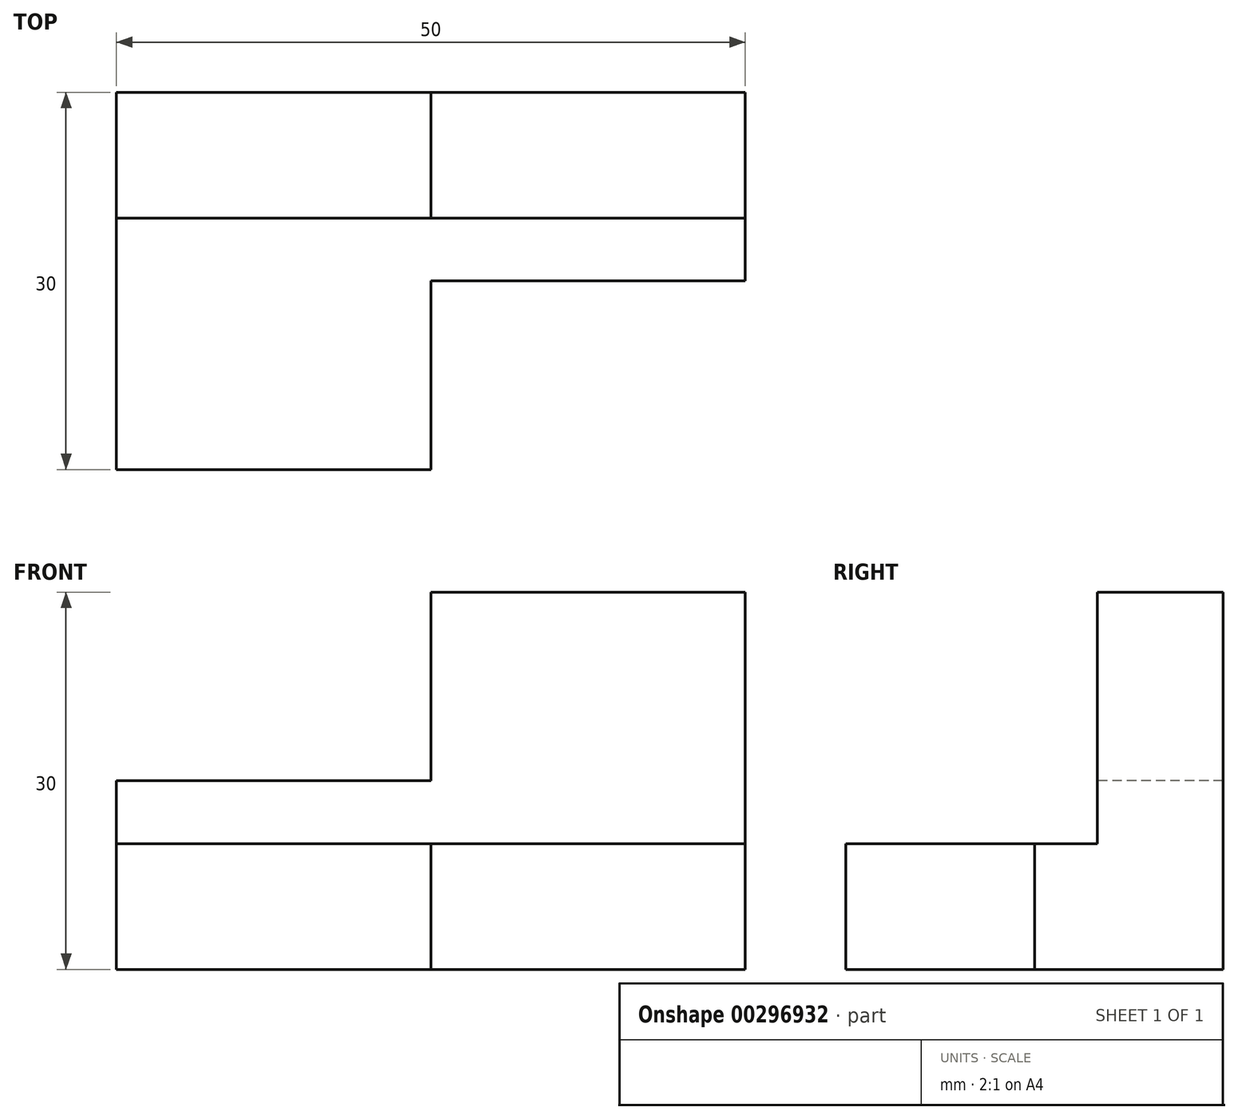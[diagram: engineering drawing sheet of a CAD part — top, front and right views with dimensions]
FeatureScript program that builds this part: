
annotation { "Feature Type Name" : "Feature", "Feature Type Description" : "" }
export const myFeature = defineFeature(function(context is Context, id is Id, definition is map)
    precondition{}
    {
        {
            var Q0;
            Q0=qCreatedBy(makeId("Right.planeOp"),FACE);
            var sketch = newSketch(context, id + "F0", { "sketchPlane" : qUnion([Q0])});
            skLineSegment(sketch, "E0.bottom", {"start": v(0, 0) * mm, "end": v(30, 0) * mm});
            skLineSegment(sketch, "E0.top", {"start": v(0, 30) * mm, "end": v(30, 30) * mm});
            skLineSegment(sketch, "E0.left", {"start": v(0, 0) * mm, "end": v(0, 30) * mm});
            skLineSegment(sketch, "E0.right", {"start": v(30, 0) * mm, "end": v(30, 30) * mm});
            skLineSegment(sketch, "E1.bottom", {"start": v(0, 30) * mm, "end": v(20, 30) * mm});
            skLineSegment(sketch, "E1.top", {"start": v(0, 10) * mm, "end": v(20, 10) * mm});
            skLineSegment(sketch, "E1.left", {"start": v(0, 30) * mm, "end": v(0, 10) * mm});
            skLineSegment(sketch, "E1.right", {"start": v(20, 30) * mm, "end": v(20, 10) * mm});
            skSolve(sketch);
        }
        {
            var Q0;
            Q0=makeQuery(id+"F0.imprint","IMPRINT",FACE,{"disambiguationData":[TD([[makeQuery(id+"F0.imprint","IMPRINT",EDGE,{"derivedFrom":sQuery(id+"F0.wireOp",EDGE,"E0.bottom")}),1.0]])]});
            extrude(context, id + "F1", {"entities" : qUnion([Q0]), "depth" : 50 * mm});
        }
        {
            var Q0;
            Q0=makeQuery(id+"F1.opExtrude","SWEPT_FACE",FACE,{"disambiguationData":[OSD([sQuery(id+"F0.wireOp",EDGE,"E1.right")])]});
            var sketch = newSketch(context, id + "F2", { "sketchPlane" : qUnion([Q0])});
            skPoint(sketch, "E2.oppositeSnap0", {"position": v(25, 30) * mm});
            skLineSegment(sketch, "E2.bottom", {"start": v(0, 30) * mm, "end": v(25, 30) * mm});
            skLineSegment(sketch, "E2.top", {"start": v(0, 15) * mm, "end": v(25, 15) * mm});
            skLineSegment(sketch, "E2.left", {"start": v(0, 30) * mm, "end": v(0, 15) * mm});
            skLineSegment(sketch, "E2.right", {"start": v(25, 30) * mm, "end": v(25, 15) * mm});
            skSolve(sketch);
        }
        {
            var Q0;
            Q0 = qSketchRegion(id + "F2", true);
            extrude(context, id + "F3", {"entities" : qUnion([Q0]), "operationType" : NewBodyOperationType.REMOVE, "endBound" : BoundingType.THROUGH_ALL, "oppositeDirection" : true, "depth" : 25 * mm});
        }
        {
            var Q0;
            Q0=makeQuery(id+"F1.opExtrude","SWEPT_FACE",FACE,{"disambiguationData":[OSD([sQuery(id+"F0.wireOp",EDGE,"E1.top")])]});
            var sketch = newSketch(context, id + "F4", { "sketchPlane" : qUnion([Q0])});
            skPoint(sketch, "E3.oppositeSnap0", {"position": v(25, 0) * mm});
            skLineSegment(sketch, "E3.bottom", {"start": v(50, 0) * mm, "end": v(25, 0) * mm});
            skLineSegment(sketch, "E3.top", {"start": v(50, 15) * mm, "end": v(25, 15) * mm});
            skLineSegment(sketch, "E3.left", {"start": v(50, 0) * mm, "end": v(50, 15) * mm});
            skLineSegment(sketch, "E3.right", {"start": v(25, 0) * mm, "end": v(25, 15) * mm});
            skSolve(sketch);
        }
        {
            var Q0;
            Q0 = qSketchRegion(id + "F4", true);
            extrude(context, id + "F5", {"entities" : qUnion([Q0]), "operationType" : NewBodyOperationType.REMOVE, "endBound" : BoundingType.THROUGH_ALL, "oppositeDirection" : true, "depth" : 25 * mm});
        }
    });
